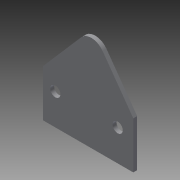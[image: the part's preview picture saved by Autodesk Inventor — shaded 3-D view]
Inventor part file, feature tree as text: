
AUTODESK INVENTOR PART (.ipt)
format: ipt  version: 2014 SP1 (Build 180222100, 222)  size: 95,232 bytes
history: native  units: in
note: dims shown in document units (in); Inventor stores cm internally (conversion verified against a paired STEP export)
features: extrude x2, sketch x2, reference x1
ambient origin geometry x8: Origin, YZ Plane, XZ Plane, XY Plane, X Axis, Y Axis, Z Axis, Center Point
bodies: Solid1 (feature_tree)
feature tree (5):
  extrude  "Extrusion1"  Depth=0.164in
  extrude  "Extrusion2"  Depth=1.0in
  sketch  "Sketch1"  dims[d0=0.164in d1=0.164in]
  reference  "Reference1"
  sketch  "Sketch2"  dims[d3=0.0625in d4=0.0in d5=0.5in d6=0.25in d7=0.2in d8=0.44in d9=0.25in d10=1.0in d11=0.19in d12=1.0in d13=0.0in]
